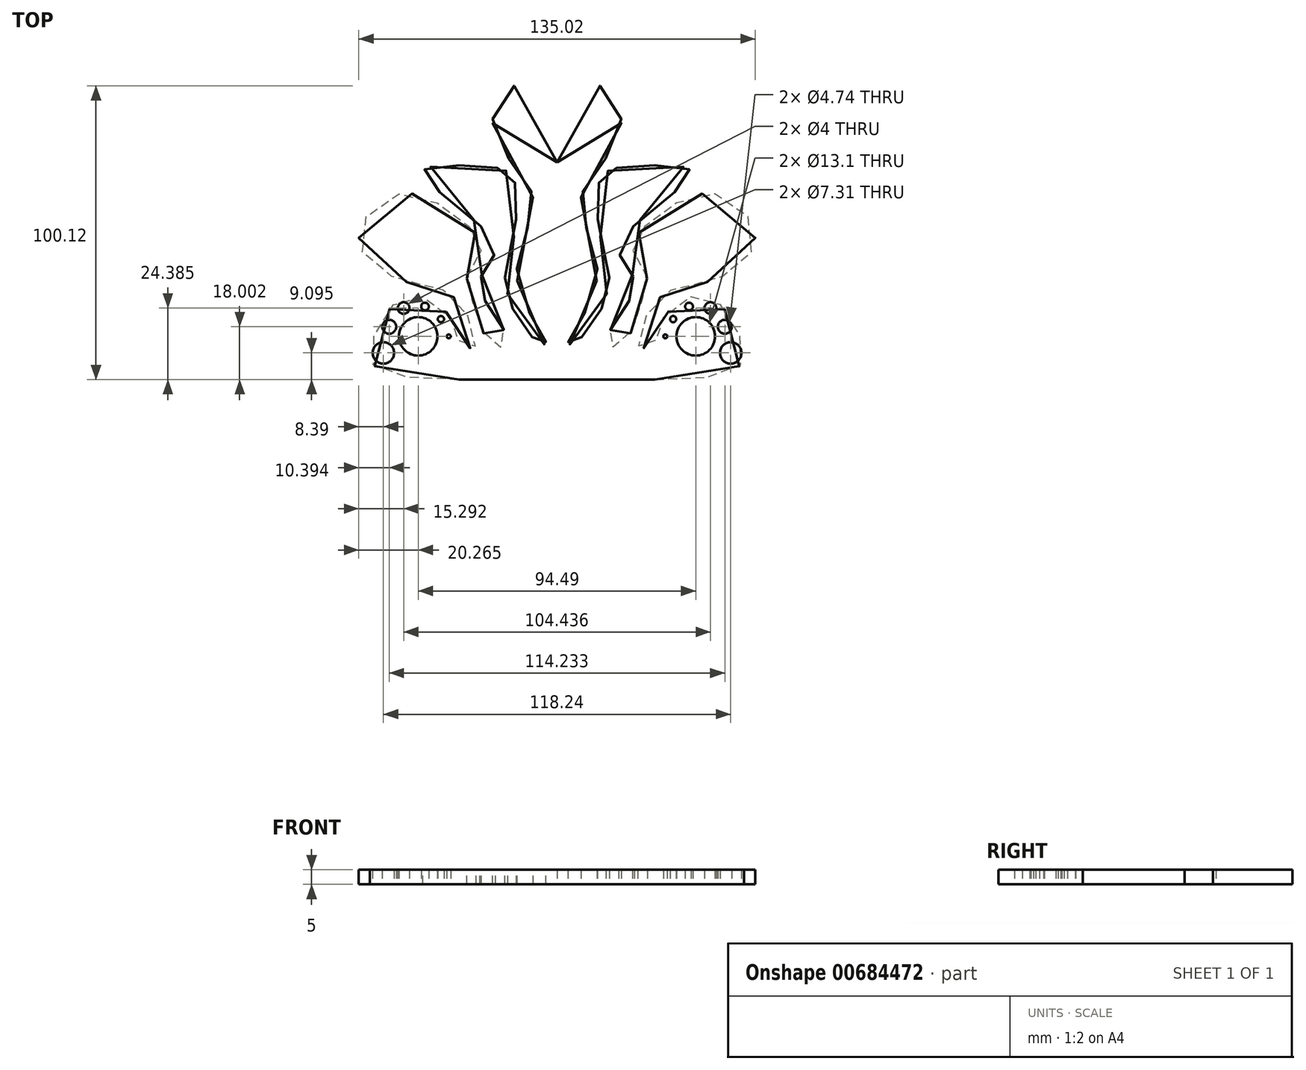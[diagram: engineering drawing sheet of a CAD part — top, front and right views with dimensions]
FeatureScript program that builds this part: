
annotation { "Feature Type Name" : "Feature", "Feature Type Description" : "" }
export const myFeature = defineFeature(function(context is Context, id is Id, definition is map)
    precondition{}
    {
        {
            var Q0;
            Q0=qCreatedBy(makeId("Front.planeOp"),FACE);
            var sketch = newSketch(context, id + "F0", { "sketchPlane" : qUnion([Q0])});
            skLineSegment(sketch, "E0", {"start": v(0, 0) * mm, "end": v(-33.3, 0) * mm});
            skFitSpline(sketch, "E1", {"points": [v(-33.3, 0) * mm, v(-62.15, 4.7) * mm, v(-61.24, 17.28) * mm, v(-49.1, 28.73) * mm, v(-35.6, 20.03) * mm, v(-33.3, 12.93) * mm, v(-28.04, 11.1) * mm, v(-33.3, 26.21) * mm, v(-44.3, 32.16) * mm, v(-53.45, 34) * mm, v(-67.42, 46.82) * mm, v(-54.83, 63.07) * mm, v(-33.3, 55.06) * mm, v(-25.75, 44.53) * mm, v(-30.56, 34.91) * mm, v(-28.04, 24.84) * mm, v(-22.1, 11.79) * mm, v(-16.83, 12.48) * mm, v(-24.15, 26.21) * mm, v(-25.3, 36.51) * mm, v(-21.4, 46.59) * mm, v(-45.67, 70.4) * mm, v(-25.98, 72.68) * mm, v(-14.77, 68.33) * mm, v(-15.45, 45.44) * mm, v(-17.74, 34.22) * mm, v(-10.19, 16.14) * mm, v(-3.78, 12.25) * mm, v(-13.62, 34.45) * mm, v(-8.36, 62.84) * mm, v(-21.93, 88.63) * mm, v(0, 74.06) * mm], "startDerivative": vector(-787.57, 7.22) * mm, "endDerivative": vector(730.57, -2844.07) * mm});
            skLineSegment(sketch, "E2", {"start": v(0, 74.06) * mm, "end": v(0, 0) * mm});
            skCircle(sketch, "E3", {"center": v(-59.12, 9.1) * mm, "radius": 3.65 * mm});
            skCircle(sketch, "E4", {"center": v(-57.12, 18) * mm, "radius": 2.37 * mm});
            skCircle(sketch, "E5", {"center": v(-52.22, 24.38) * mm, "radius": 2 * mm});
            skCircle(sketch, "E6", {"center": v(-44.94, 24.9) * mm, "radius": 1.31 * mm});
            skCircle(sketch, "E7", {"center": v(-39.53, 20.6) * mm, "radius": 1.06 * mm});
            skCircle(sketch, "E8", {"center": v(-36.85, 14.74) * mm, "radius": 0.67 * mm});
            skCircle(sketch, "E9", {"center": v(-47.25, 14.74) * mm, "radius": 6.55 * mm});
            skFitSpline(sketch, "E10.MirrorCS", {"points": [v(33.3, 0) * mm, v(62.15, 4.7) * mm, v(61.24, 17.28) * mm, v(49.1, 28.73) * mm, v(35.6, 20.03) * mm, v(33.3, 12.93) * mm, v(28.04, 11.1) * mm, v(33.3, 26.21) * mm, v(44.3, 32.16) * mm, v(53.45, 34) * mm, v(67.42, 46.82) * mm, v(54.83, 63.07) * mm, v(33.3, 55.06) * mm, v(25.75, 44.53) * mm, v(30.56, 34.91) * mm, v(28.04, 24.84) * mm, v(22.1, 11.79) * mm, v(16.83, 12.48) * mm, v(24.15, 26.21) * mm, v(25.3, 36.51) * mm, v(21.4, 46.59) * mm, v(45.67, 70.4) * mm, v(25.98, 72.68) * mm, v(14.77, 68.33) * mm, v(15.45, 45.44) * mm, v(17.74, 34.22) * mm, v(10.19, 16.14) * mm, v(3.78, 12.25) * mm, v(13.62, 34.45) * mm, v(8.36, 62.84) * mm, v(21.93, 88.63) * mm, v(0, 74.06) * mm], "startDerivative": vector(787.57, 7.22) * mm, "endDerivative": vector(-730.57, -2844.07) * mm});
            skCircle(sketch, "E11.MirrorC", {"center": v(59.12, 9.1) * mm, "radius": 3.65 * mm});
            skCircle(sketch, "E12.MirrorC", {"center": v(57.12, 18) * mm, "radius": 2.37 * mm});
            skCircle(sketch, "E13.MirrorC", {"center": v(52.22, 24.38) * mm, "radius": 2 * mm});
            skCircle(sketch, "E14.MirrorC", {"center": v(44.94, 24.9) * mm, "radius": 1.31 * mm});
            skCircle(sketch, "E15.MirrorC", {"center": v(39.53, 20.6) * mm, "radius": 1.06 * mm});
            skCircle(sketch, "E16.MirrorC", {"center": v(36.85, 14.74) * mm, "radius": 0.67 * mm});
            skCircle(sketch, "E17.MirrorC", {"center": v(47.25, 14.74) * mm, "radius": 6.55 * mm});
            skLineSegment(sketch, "E18", {"start": v(0, 0) * mm, "end": v(33.3, 0) * mm});
            skSolve(sketch);
        }
        {
            var Q0;
            Q0=makeQuery(id+"F0.imprint","IMPRINT",FACE,{"disambiguationData":[TD([[makeQuery(id+"F0.imprint","IMPRINT",EDGE,{"derivedFrom":sQuery(id+"F0.wireOp",EDGE,"E0")}),-1.0]])]});
            var Q1;
            Q1=makeQuery(id+"F0.imprint","IMPRINT",FACE,{"disambiguationData":[TD([[makeQuery(id+"F0.imprint","IMPRINT",EDGE,{"derivedFrom":sQuery(id+"F0.wireOp",EDGE,"E2")}),1.0]])]});
            extrude(context, id + "F1", {"entities" : qUnion([Q0, Q1]), "depth" : 5 * mm, "offsetDistance" : 25 * mm});
        }
        {
            var Q0;
            Q0=makeQuery(id+"F1.opExtrude","SWEPT_BODY",BODY,{"disambiguationData":[OSD([sQuery(id+"F0.wireOp",EDGE,"E0"),sQuery(id+"F0.wireOp",EDGE,"E1"),sQuery(id+"F0.wireOp",EDGE,"E3"),sQuery(id+"F0.wireOp",EDGE,"E4"),sQuery(id+"F0.wireOp",EDGE,"E5"),sQuery(id+"F0.wireOp",EDGE,"E6"),sQuery(id+"F0.wireOp",EDGE,"E7"),sQuery(id+"F0.wireOp",EDGE,"E8"),sQuery(id+"F0.wireOp",EDGE,"E9"),sQuery(id+"F0.wireOp",EDGE,"E10.MirrorCS"),sQuery(id+"F0.wireOp",EDGE,"E11.MirrorC"),sQuery(id+"F0.wireOp",EDGE,"E12.MirrorC"),sQuery(id+"F0.wireOp",EDGE,"E13.MirrorC"),sQuery(id+"F0.wireOp",EDGE,"E14.MirrorC"),sQuery(id+"F0.wireOp",EDGE,"E15.MirrorC"),sQuery(id+"F0.wireOp",EDGE,"E16.MirrorC"),sQuery(id+"F0.wireOp",EDGE,"E17.MirrorC"),sQuery(id+"F0.wireOp",EDGE,"E18")])]});
            var Q1;
            Q1=makeQuery(id+"F1.opExtrude","CAP_EDGE",EDGE,{"disambiguationData":[OSD([sQuery(id+"F0.wireOp",EDGE,"E0"),sQuery(id+"F0.wireOp",EDGE,"E18")])],"isStart":true});
            transform(context, id + "F2", {"entities" : qUnion([Q0]), "transformType" : TransformType.ROTATION, "transformAxis" : qUnion([Q1]), "angle" : 90 * degree, "makeCopy" : false});
        }
    });
